# Revit family: NaughtOne_PullmanDeskNOPUL
name_source: partatom
category: Furniture
units: mm (PartAtom-declared; Revit-internal decimal feet)

## family parameters
Always vertical = Yes
Cut with Voids When Loaded = No
Enable Cutting in Views = No
OmniClass Number = 23.40.20.00
OmniClass Title = General Furniture and Specialties
Render Appearance Source = Family Geometry
Room Calculation Point = No
Shared = Yes
Work Plane-Based = No

## types (12) — shared parameters
Assembly Code = E2020200
Catalog = naughtone
Export Type to IFC As = IfcFurnishingElementType
Keynote = Pr_40_50_12
ManufacturerAddress = Knaresborough Tech Park, Manse Lane, Knaresborough, HG5 8LF
ManufacturerName = Naughtone
Package Qty = 1
Product Documentation Link = http://www.naughtone.com
Type IFC Predefined Type = BOOTH
URL = www.naughtone.com
zero-valued in all types: Default Elevation

## per-type parameters (varying)
| type | Actual Depth | Actual Width | Depth | Description | Model | Pod L1 | Pod L2 | Pod R1 | Pod R2 | Switch L | Switch R | Table Top 1 | Table Top 2 | Type | Width |
| Desk 30d 59w 29d 57w surf size electric std range single fabric | 31.899 " | 63.237 " | 30 " | Pullman Ht Adj Desk desk 30d 59w 29d 57w surf size electric std range single fabric | NOPHTD00LE1 | No | No | No | No | Yes | No | Yes | No | 1 | 59 " |
| Desk 30d 59w 29d 57w surf size electric std range multi fabrics | 31.899 " | 63.237 " | 30 " | Pullman Ht Adj Desk desk 30d 59w 29d 57w surf size electric std range multi fabrics | NOPHTD00LE2 | No | No | No | No | Yes | No | Yes | No | 1 | 59 " |
| Desk 25.5d 47w 24.5d 45w surf size electric std range single fabric | 27.399 " | 51.237 " | 25.5 " | Pullman Ht Adj Desk desk 25.5d 47w 24.5d 45w surf size electric std range single fabric | NOPHTD00SE1 | No | No | No | No | Yes | No | No | Yes | 2 | 47 " |
| Desk 25.5d 47w 24.5d 45w surf size electric std range multi fabrics | 27.399 " | 51.237 " | 25.5 " | Pullman Ht Adj Desk desk 25.5d 47w 24.5d 45w surf size electric std range multi fabrics | NOPHTD00SE2 | No | No | No | No | Yes | No | No | Yes | 2 | 47 " |
| Desk pod  access lf 30d 59w 29d 57w surf size electric std range single fabric | 31.899 " | 63.237 " | 30 " | Pullman Ht Adj Desk desk pod  access lf 30d 59w 29d 57w surf size electric std range single fabric | NOPHTDPLLE1 | No | No | Yes | No | Yes | No | Yes | No | 3 | 59 " |
| Desk pod  access lf 30d 59w 29d 57w surf size electric std range multi fabrics | 31.899 " | 63.237 " | 30 " | Pullman Ht Adj Desk desk pod  access lf 30d 59w 29d 57w surf size electric std range multi fabrics | NOPHTDPLLE2 | No | No | Yes | No | Yes | No | Yes | No | 3 | 59 " |
| Desk pod  access lf 25.5d 47w 24.5d 45w surf size electric std range single fabric | 27.399 " | 51.237 " | 25.5 " | Pullman Ht Adj Desk desk pod  access lf 25.5d 47w 24.5d 45w surf size electric std range single fabric | NOPHTDPLSE1 | No | No | No | Yes | Yes | No | No | Yes | 4 | 47 " |
| Desk pod  access lf 25.5d 47w 24.5d 45w surf size electric std range multi fabrics | 27.399 " | 51.237 " | 25.5 " | Pullman Ht Adj Desk desk pod  access lf 25.5d 47w 24.5d 45w surf size electric std range multi fabrics | NOPHTDPLSE2 | No | No | No | Yes | Yes | No | No | Yes | 4 | 47 " |
| Desk pod  access rt 30d 59w 29d 57w surf size electric std range single fabric | 31.899 " | 63.237 " | 30 " | Pullman Ht Adj Desk desk pod  access rt 30d 59w 29d 57w surf size electric std range single fabric | NOPHTDPRLE1 | Yes | No | No | No | No | Yes | Yes | No | 5 | 59 " |
| Desk pod  access rt 30d 59w 29d 57w surf size electric std range multi fabrics | 31.899 " | 63.237 " | 30 " | Pullman Ht Adj Desk desk pod  access rt 30d 59w 29d 57w surf size electric std range multi fabrics | NOPHTDPRLE2 | Yes | No | No | No | No | Yes | Yes | No | 5 | 59 " |
| Desk pod access rt 25.5d  47w 24.5d 45w surf size electric std range single fabric | 27.399 " | 51.237 " | 25.5 " | Pullman Ht Adj Desk desk pod access rt 25.5d  47w 24.5d 45w surf size electric std range single fabric | NOPHTDPRSE | No | Yes | No | No | No | Yes | No | Yes | 6 | 47 " |
| Desk pod  access rt 25.5d 47w 24.5d 45w surf size electric std range single fabric | 27.399 " | 51.237 " | 25.5 " | Pullman Ht Adj Desk desk pod  access rt 25.5d 47w 24.5d 45w surf size electric std range single fabric | NOPHTDPRSE1 | No | Yes | No | No | No | Yes | No | Yes | 6 | 47 " |

## geometry (parser evidence)
native form markers: Sweep x24
no freeform markers — native parametric forms only
